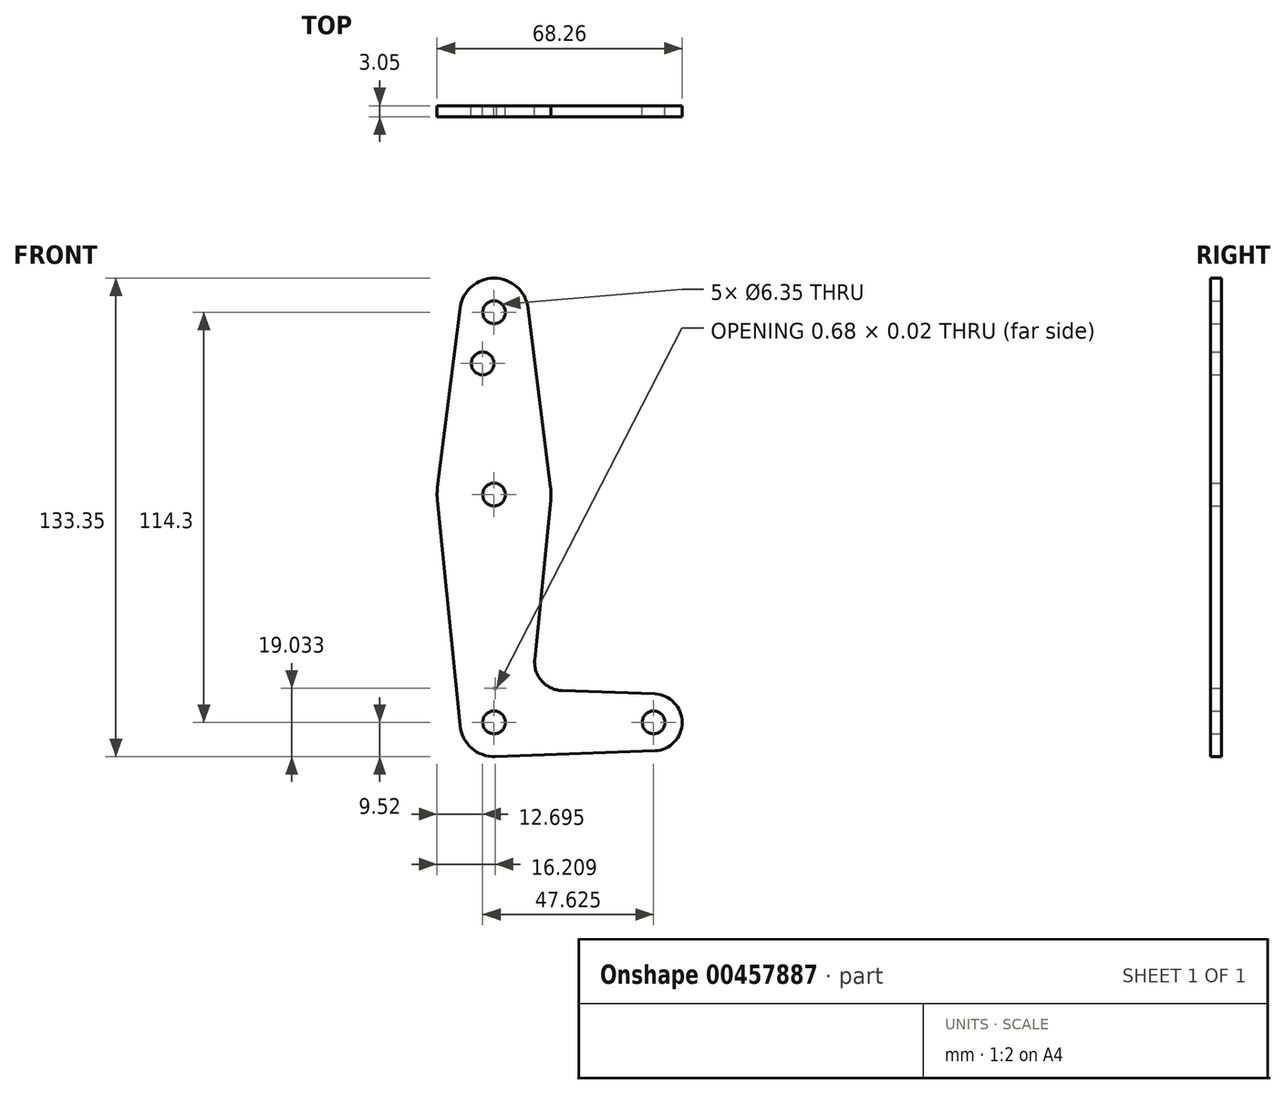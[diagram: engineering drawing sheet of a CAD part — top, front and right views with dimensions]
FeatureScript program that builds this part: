
annotation { "Feature Type Name" : "Feature", "Feature Type Description" : "" }
export const myFeature = defineFeature(function(context is Context, id is Id, definition is map)
    precondition{}
    {
        {
            var Q0;
            Q0=qCreatedBy(makeId("Front.planeOp"),FACE);
            var sketch = newSketch(context, id + "F0", { "sketchPlane" : qUnion([Q0])});
            skLineSegment(sketch, "E0", {"start": v(0, 0) * mm, "end": v(0, 114.3) * mm, "construction": true});
            skLineSegment(sketch, "E1", {"start": v(0, 0) * mm, "end": v(44.45, 0) * mm, "construction": true});
            skCircle(sketch, "E2", {"center": v(0, 114.3) * mm, "radius": 9.53 * mm});
            skCircle(sketch, "E3", {"center": v(44.45, 0) * mm, "radius": 7.94 * mm});
            skCircle(sketch, "E4", {"center": v(0, 0) * mm, "radius": 9.53 * mm});
            skCircle(sketch, "E5", {"center": v(0, 63.5) * mm, "radius": 15.88 * mm});
            skLineSegment(sketch, "E6", {"start": v(-9.45, 115.5) * mm, "end": v(-15.75, 65.48) * mm});
            skLineSegment(sketch, "E7.MirrorCS", {"start": v(9.45, 115.5) * mm, "end": v(15.75, 65.48) * mm});
            skLineSegment(sketch, "E8.MirrorCS", {"start": v(0, 9.53) * mm, "end": v(0.68, 9.5) * mm});
            skCircle(sketch, "E9", {"center": v(0, 114.3) * mm, "radius": 3.18 * mm});
            skCircle(sketch, "E10", {"center": v(0, 63.5) * mm, "radius": 3.18 * mm});
            skCircle(sketch, "E11", {"center": v(0, 0) * mm, "radius": 3.18 * mm});
            skCircle(sketch, "E12", {"center": v(44.45, 0) * mm, "radius": 3.18 * mm});
            skCircle(sketch, "E13", {"center": v(-3.18, 100.03) * mm, "radius": 3.18 * mm});
            skPoint(sketch, "E14.orphan", {"position": v(9.57, 0) * mm});
            skLineSegment(sketch, "E15", {"start": v(-9.48, -0.95) * mm, "end": v(-15.8, 61.91) * mm});
            skLineSegment(sketch, "E16.MirrorCS", {"start": v(11.34, 17.6) * mm, "end": v(15.8, 61.91) * mm});
            skLineSegment(sketch, "E17", {"start": v(0.34, -9.52) * mm, "end": v(44.73, -7.93) * mm});
            skLineSegment(sketch, "E18.MirrorCS", {"start": v(18.97, 8.85) * mm, "end": v(44.73, 7.93) * mm});
            skPoint(sketch, "E19.newPointA", {"position": v(9.48, -0.95) * mm});
            skPoint(sketch, "E19.newPointB", {"position": v(0.34, 9.52) * mm});
            skArc(sketch, "E19.filletArc", {"start": v(11.34, 17.6) * mm, "mid": v(13.26, 11.57) * mm, "end": v(18.97, 8.85) * mm});
            skSolve(sketch);
        }
        {
            var Q0;
            Q0=makeQuery(id+"F0.imprint","IMPRINT",FACE,{"disambiguationData":[TD([[makeQuery(id+"F0.imprint","IMPRINT",EDGE,{"derivedFrom":sQuery(id+"F0.wireOp",EDGE,"E9")}),-1.0]])]});
            var Q1;
            {var subQ0=sQuery(id+"F0.wireOp",EDGE,"E6");Q1=makeQuery(id+"F0.imprint","IMPRINT",FACE,{"disambiguationData":[TD([[makeQuery(id+"F0.imprint","IMPRINT",EDGE,{"derivedFrom":subQ0}),1.0]])]});}
            var Q2;
            Q2=makeQuery(id+"F0.imprint","IMPRINT",FACE,{"disambiguationData":[TD([[makeQuery(id+"F0.imprint","IMPRINT",EDGE,{"derivedFrom":sQuery(id+"F0.wireOp",EDGE,"E10")}),-1.0]])]});
            var Q3;
            {var subQ4=sQuery(id+"F0.wireOp",EDGE,"E15");Q3=makeQuery(id+"F0.imprint","IMPRINT",FACE,{"disambiguationData":[TD([[makeQuery(id+"F0.imprint","IMPRINT",EDGE,{"derivedFrom":subQ4}),-1.0]])]});}
            var Q4;
            {var subQ0=sQuery(id+"F0.wireOp",EDGE,"E8.MirrorCS");Q4=makeQuery(id+"F0.imprint","IMPRINT",FACE,{"disambiguationData":[TD([[makeQuery(id+"F0.imprint","IMPRINT",EDGE,{"derivedFrom":subQ0}),-1.0]])]});}
            var Q5;
            Q5=makeQuery(id+"F0.imprint","IMPRINT",FACE,{"disambiguationData":[TD([[makeQuery(id+"F0.imprint","IMPRINT",EDGE,{"derivedFrom":sQuery(id+"F0.wireOp",EDGE,"E12")}),-1.0]])]});
            extrude(context, id + "F1", {"entities" : qUnion([Q0, Q1, Q2, Q3, Q4, Q5]), "depth" : 3.05 * mm});
        }
    });
